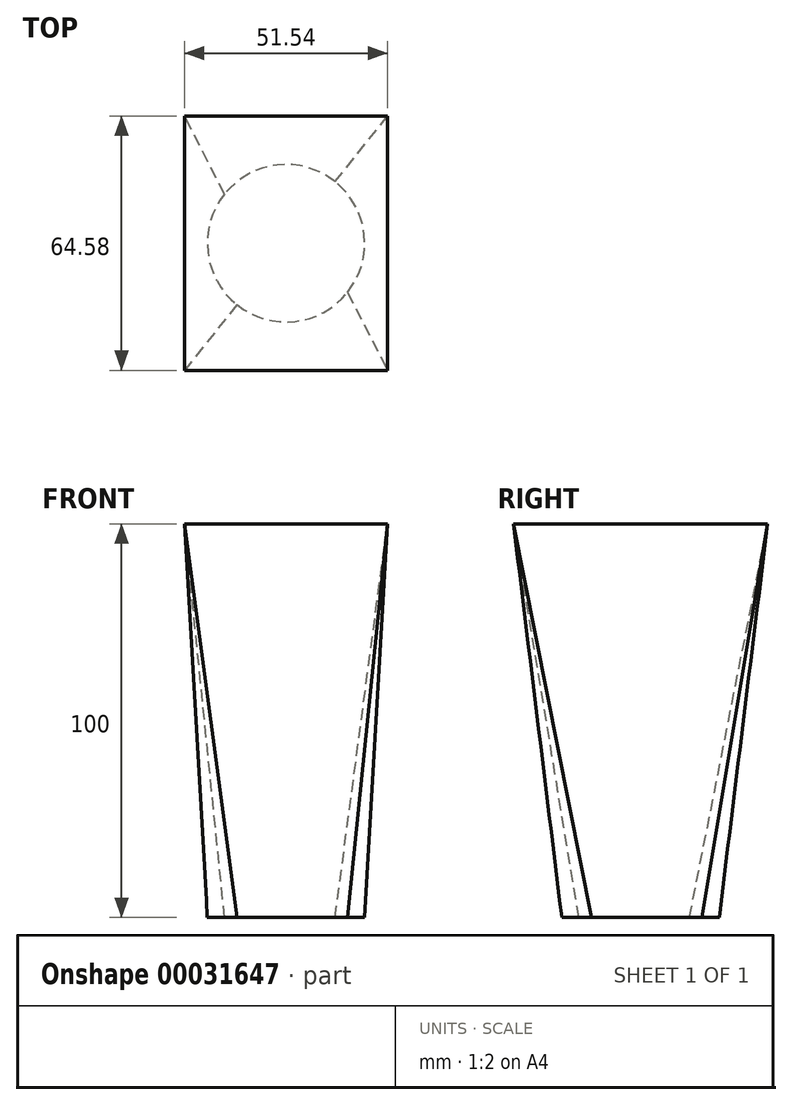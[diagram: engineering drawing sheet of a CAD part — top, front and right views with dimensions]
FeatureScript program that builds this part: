
annotation { "Feature Type Name" : "Feature", "Feature Type Description" : "" }
export const myFeature = defineFeature(function(context is Context, id is Id, definition is map)
    precondition{}
    {
        {
            var Q0;
            Q0=qCreatedBy(makeId("Top.planeOp"),FACE);
            var sketch = newSketch(context, id + "F0", { "sketchPlane" : qUnion([Q0])});
            skCircle(sketch, "E0", {"center": v(0, 0) * mm, "radius": 20 * mm});
            skSolve(sketch);
        }
        {
            var Q0;
            Q0=qCreatedBy(makeId("Top.planeOp"),FACE);
            cPlane(context, id + "F1", {"entities" : qUnion([Q0]), "cplaneType" : CPlaneType.OFFSET, "offset" : 100 * mm, "width" : 150 * mm, "height" : 150 * mm});
        }
        {
            var Q0;
            Q0=qCreatedBy(id+"F1.planeOp",FACE);
            var sketch = newSketch(context, id + "F2", { "sketchPlane" : qUnion([Q0])});
            skLineSegment(sketch, "E1.rect.bottom", {"start": v(25.77, 32.29) * mm, "end": v(-25.77, 32.29) * mm});
            skLineSegment(sketch, "E1.rect.top", {"start": v(25.77, -32.29) * mm, "end": v(-25.77, -32.29) * mm});
            skLineSegment(sketch, "E1.rect.left", {"start": v(25.77, 32.29) * mm, "end": v(25.77, -32.29) * mm});
            skLineSegment(sketch, "E1.rect.right", {"start": v(-25.77, 32.29) * mm, "end": v(-25.77, -32.29) * mm});
            skPoint(sketch, "E1.rect.middle", {"position": v(0, 0) * mm});
            skSolve(sketch);
        }
        {
            var Q0;
            Q0=makeQuery(id+"F0.imprint","IMPRINT",FACE,{"disambiguationData":[TD([[makeQuery(id+"F0.imprint","IMPRINT",EDGE,{"derivedFrom":sQuery(id+"F0.wireOp",EDGE,"E0")}),1.0]])]});
            var Q1;
            Q1=makeQuery(id+"F2.imprint","IMPRINT",FACE,{"disambiguationData":[TD([[makeQuery(id+"F2.imprint","IMPRINT",EDGE,{"derivedFrom":sQuery(id+"F2.wireOp",EDGE,"E1.rect.bottom")}),1.0]])]});
            loft(context, id + "F3", {"sheetProfilesArray" : [{ "sheetProfileEntities" : qUnion([Q0]) }, { "sheetProfileEntities" : qUnion([Q1]) }]});
        }
    });
